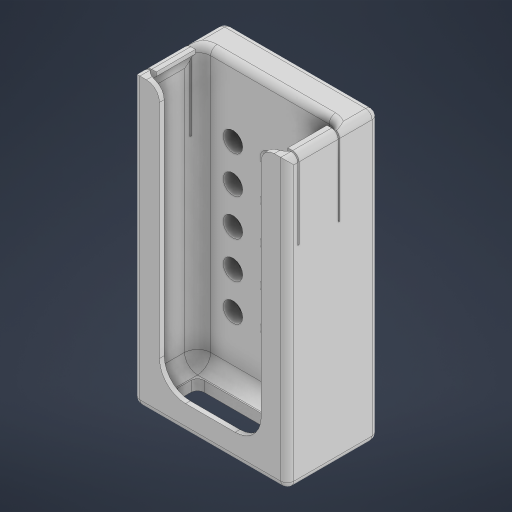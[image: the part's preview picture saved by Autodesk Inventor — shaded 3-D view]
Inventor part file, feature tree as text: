
AUTODESK INVENTOR PART (.ipt)
format: ipt  version: 2023 (Build 270158000, 158)  size: 403,968 bytes
history: native  units: in
note: dims shown in document units (in); Inventor stores cm internally (conversion verified against a paired STEP export)
features: sketch x7, extrude x6, fillet x4, projected_geometry x2, mirror x1, hole x1, pattern_linear x1
ambient origin geometry x8: Origin, YZ Plane, XZ Plane, XY Plane, X Axis, Y Axis, Z Axis, Center Point
bodies: Solid1 (feature_tree)
feature tree (22):
  extrude  "Extrusion1"  Depth=5.3in
  extrude  "Extrusion2"  Depth=1.75in TaperAngle=0.0deg
  extrude  "Extrusion3"  Depth=0.09in
  fillet  "Fillet1"  Radius=0.09in
  extrude  "Extrusion4"  Depth=5.3in TaperAngle=0.0deg
  extrude  "Extrusion5"  Depth=0.5in
  mirror  "Mirror1"
  extrude  "Extrusion6"  Depth=0.5in TaperAngle=0.0deg
  hole  "Hole1"  [1 undecoded]
  pattern_linear  "Rectangular Pattern1"  Spacing1=0.025in  [1 undecoded]
  fillet  "Fillet2"  Radius=0.025in
  fillet  "Fillet3"  Radius=0.75in
  fillet  "Fillet4"  Radius=1.5in
  sketch  "Sketch1"  dims[d0=2.75in d1=5.3in]
  sketch  "Sketch2"  dims[d2=0.1in d3=1.75in d4=0.0in]
  sketch  "Sketch3"  dims[d5=0.09in d6=0.09in d7=0.09in]
  sketch  "Sketch4"  dims[d8=1.05in d9=5.3in d10=0.0in]
  sketch  "Sketch5"  dims[d11=0.5in d12=0.5in]
  projected_geometry  "Projected Loop1"
  sketch  "Sketch6"  dims[d13=0.5in d14=5.25in d15=0.0in]
  projected_geometry  "Projected Loop2"
  sketch  "Sketch7"  dims[d16=0.25in d17=0.2in d18=0.025in d19=0.025in d20=0.75in d21=1.5in d22=0.0in d23=0.0in d30=1.0in d31=0.0in d32=0.125in d33=0.05in d35=0.375in d36=0.375in d37=0.025in d38=0.025in d39=1.0in d40=0.0in d42=0.707in d43=1.414in d44=0.156in d45=0.38in d46=0.375in d47=0.25in d48=0.5635in d49=1.0in d50=0.8108in d51=1.1811in d53=0.707in d54=1.9685in d56=0.707in d57=0.5in d58=0.25in d59=0.125in]
note: 2 required parameter values undecoded (feature->parameter linkage not recoverable at this tier; creation-order binding heuristic only, values carry confidence <= 0.55)
